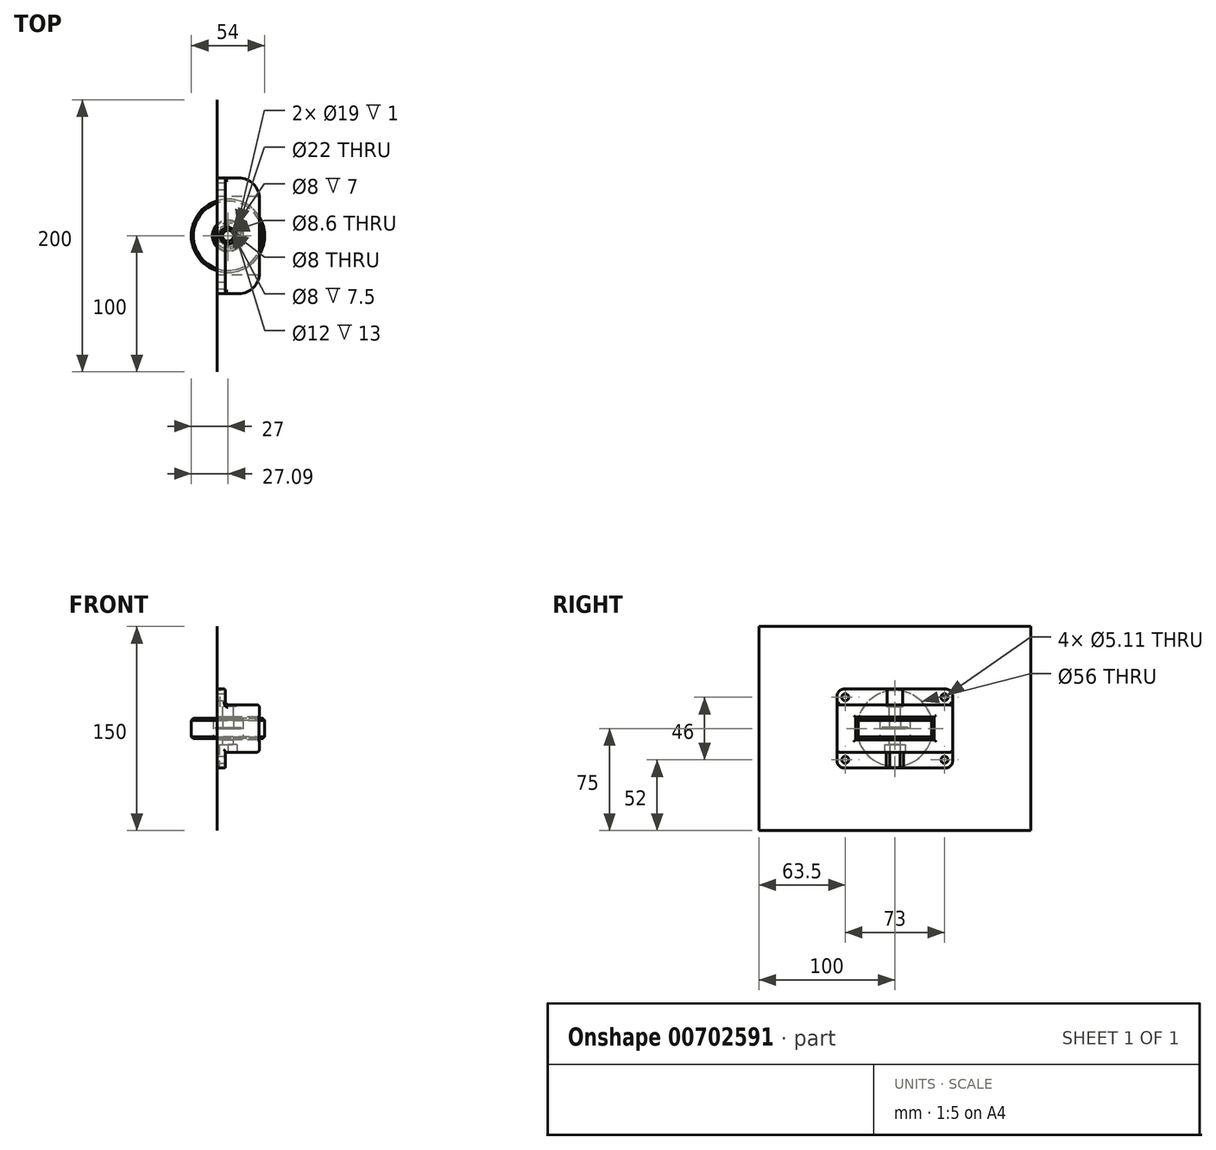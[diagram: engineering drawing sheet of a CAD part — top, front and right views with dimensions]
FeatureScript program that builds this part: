
annotation { "Feature Type Name" : "Feature", "Feature Type Description" : "" }
export const myFeature = defineFeature(function(context is Context, id is Id, definition is map)
    precondition{}
    {
        {
            var Q0;
            Q0=qCreatedBy(makeId("Right.planeOp"),FACE);
            var sketch = newSketch(context, id + "F0", { "sketchPlane" : qUnion([Q0])});
            skLineSegment(sketch, "E0.bottom", {"start": v(100, 75) * mm, "end": v(-100, 75) * mm});
            skLineSegment(sketch, "E0.top", {"start": v(100, -75) * mm, "end": v(-100, -75) * mm});
            skLineSegment(sketch, "E0.left", {"start": v(100, 75) * mm, "end": v(100, -75) * mm});
            skLineSegment(sketch, "E0.right", {"start": v(-100, 75) * mm, "end": v(-100, -75) * mm});
            skPoint(sketch, "E0.middle", {"position": v(0, 0) * mm});
            skCircle(sketch, "E1", {"center": v(0, 0) * mm, "radius": 28 * mm});
            skSolve(sketch);
        }
        {
            var Q0;
            Q0=makeQuery(id+"F0.imprint","IMPRINT",FACE,{"disambiguationData":[TD([[makeQuery(id+"F0.imprint","IMPRINT",EDGE,{"derivedFrom":sQuery(id+"F0.wireOp",EDGE,"E0.bottom")}),1.0]])]});
            extrude(context, id + "F1", {"entities" : qUnion([Q0]), "oppositeDirection" : true, "depth" : 3 / 203.2 * mm, "offsetDistance" : 25 * mm});
        }
        {
            var Q0;
            Q0=qCreatedBy(makeId("Top.planeOp"),FACE);
            var sketch = newSketch(context, id + "F2", { "sketchPlane" : qUnion([Q0])});
            skCircle(sketch, "E2", {"center": v(8, 0) * mm, "radius": 4 * mm});
            skCircle(sketch, "E3", {"center": v(8, 0) * mm, "radius": 11 * mm});
            skLineSegment(sketch, "E4", {"start": v(-49.17, 0) * mm, "end": v(42.17, 0) * mm, "construction": true});
            skLineSegment(sketch, "E5", {"start": v(-9.33, 54.74) * mm, "end": v(-9.33, -36.6) * mm, "construction": true});
            skSolve(sketch);
        }
        {
            var Q0;
            Q0=makeQuery(id+"F2.imprint","IMPRINT",FACE,{"disambiguationData":[TD([[makeQuery(id+"F2.imprint","IMPRINT",EDGE,{"derivedFrom":sQuery(id+"F2.wireOp",EDGE,"E2")}),-1.0]])]});
            extrude(context, id + "F3", {"entities" : qUnion([Q0]), "depth" : 7 * mm, "offsetDistance" : 25 * mm});
        }
        {
            var Q0;
            Q0=makeQuery(id+"F3.opExtrude","CAP_FACE",FACE,{"disambiguationData":[OSD([sQuery(id+"F2.wireOp",EDGE,"E2"),sQuery(id+"F2.wireOp",EDGE,"E3")])],"isStart":false});
            var sketch = newSketch(context, id + "F4", { "sketchPlane" : qUnion([Q0])});
            skCircle(sketch, "E6", {"center": v(8, 0) * mm, "radius": 5.5 * mm});
            skCircle(sketch, "E7", {"center": v(8, 0) * mm, "radius": 9.5 * mm});
            skSolve(sketch);
        }
        {
            var Q0;
            Q0=makeQuery(id+"F4.imprint","IMPRINT",FACE,{"disambiguationData":[TD([[makeQuery(id+"F4.imprint","IMPRINT",EDGE,{"derivedFrom":sQuery(id+"F4.wireOp",EDGE,"E6")}),-1.0]])]});
            extrude(context, id + "F5", {"entities" : qUnion([Q0]), "operationType" : NewBodyOperationType.REMOVE, "oppositeDirection" : true, "depth" : 1 * mm, "offsetDistance" : 25 * mm});
        }
        {
            var Q0;
            Q0=makeQuery(id+"F3.opExtrude","CAP_FACE",FACE,{"disambiguationData":[OSD([sQuery(id+"F2.wireOp",EDGE,"E2"),sQuery(id+"F2.wireOp",EDGE,"E3")])],"isStart":true});
            var sketch = newSketch(context, id + "F6", { "sketchPlane" : qUnion([Q0])});
            skCircle(sketch, "E8", {"center": v(8, 0) * mm, "radius": 5.5 * mm});
            skCircle(sketch, "E9", {"center": v(8, 0) * mm, "radius": 9.5 * mm});
            skSolve(sketch);
        }
        {
            var Q0;
            Q0=makeQuery(id+"F6.imprint","IMPRINT",FACE,{"disambiguationData":[TD([[makeQuery(id+"F6.imprint","IMPRINT",EDGE,{"derivedFrom":sQuery(id+"F6.wireOp",EDGE,"E8")}),-1.0]])]});
            extrude(context, id + "F7", {"entities" : qUnion([Q0]), "operationType" : NewBodyOperationType.REMOVE, "oppositeDirection" : true, "depth" : 1 * mm, "offsetDistance" : 25 * mm});
        }
        {
            var Q0;
            Q0=qCreatedBy(makeId("Top.planeOp"),FACE);
            var sketch = newSketch(context, id + "F8", { "sketchPlane" : qUnion([Q0])});
            skCircle(sketch, "E10", {"center": v(7.9, 0) * mm, "radius": 27 * mm});
            skCircle(sketch, "E11", {"center": v(7.9, 0) * mm, "radius": 11 * mm});
            skSolve(sketch);
        }
        {
            var Q0;
            Q0 = qSketchRegion(id + "F8", true);
            extrude(context, id + "F9", {"entities" : qUnion([Q0]), "endBound" : BoundingType.SYMMETRIC, "depth" : 15 * mm, "offsetDistance" : 25 * mm});
        }
        {
            var Q0;
            Q0=makeQuery(id+"F9.opExtrude","CAP_EDGE",EDGE,{"disambiguationData":[OSD([sQuery(id+"F8.wireOp",EDGE,"E10")])],"isStart":false});
            var Q1;
            Q1=makeQuery(id+"F9.opExtrude","CAP_EDGE",EDGE,{"disambiguationData":[OSD([sQuery(id+"F8.wireOp",EDGE,"E10")])],"isStart":true});
            chamfer(context, id + "F10", {"entities" : qUnion([Q0, Q1]), "width" : 1.5 * mm, "tangentPropagation" : true});
        }
        {
            var Q0;
            Q0=makeQuery(id+"F0.imprint","IMPRINT",FACE,{"disambiguationData":[TD([[makeQuery(id+"F0.imprint","IMPRINT",EDGE,{"derivedFrom":sQuery(id+"F0.wireOp",EDGE,"E0.bottom")}),1.0]])]});
            var sketch = newSketch(context, id + "F11", { "sketchPlane" : qUnion([Q0])});
            skLineSegment(sketch, "E12.bottom", {"start": v(-42.5, 29) * mm, "end": v(42.5, 29) * mm});
            skLineSegment(sketch, "E12.top", {"start": v(-42.5, -29) * mm, "end": v(42.5, -29) * mm});
            skLineSegment(sketch, "E12.left", {"start": v(-42.5, 29) * mm, "end": v(-42.5, -29) * mm});
            skLineSegment(sketch, "E12.right", {"start": v(42.5, 29) * mm, "end": v(42.5, -29) * mm});
            skPoint(sketch, "E12.middle", {"position": v(0, 0) * mm});
            skLineSegment(sketch, "E13.bottom", {"start": v(29, 8.5) * mm, "end": v(-29, 8.5) * mm});
            skLineSegment(sketch, "E13.top", {"start": v(29, -8.5) * mm, "end": v(-29, -8.5) * mm});
            skLineSegment(sketch, "E13.left", {"start": v(29, 8.5) * mm, "end": v(29, -8.5) * mm});
            skLineSegment(sketch, "E13.right", {"start": v(-29, 8.5) * mm, "end": v(-29, -8.5) * mm});
            skSolve(sketch);
        }
        {
            var Q0;
            Q0=makeQuery(id+"F11.imprint","IMPRINT",FACE,{"disambiguationData":[TD([[makeQuery(id+"F11.imprint","IMPRINT",EDGE,{"derivedFrom":sQuery(id+"F11.wireOp",EDGE,"E12.bottom")}),-1.0]])]});
            var Q1;
            {var subQ0=sQuery(id+"F11.wireOp",EDGE,"E13.bottom");var subQ1=makeQuery(id+"F0.imprint","IMPRINT",EDGE,{"derivedFrom":sQuery(id+"F0.wireOp",EDGE,"E1")});var subQ2=makeQuery(id+"F11.imprint","INTERSECT",VERTEX,{"disambiguationData":[OD(0.0)],"derivedFrom":[subQ1,subQ0]});Q1=makeQuery(id+"F11.imprint","IMPRINT",FACE,{"disambiguationData":[TD([[makeQuery(id+"F11.imprint","IMPRINT",EDGE,{"disambiguationData":[TD([[subQ2,-1.0]])],"derivedFrom":subQ0}),-1.0]])]});}
            var Q2;
            {var subQ0=sQuery(id+"F11.wireOp",EDGE,"E13.top");var subQ1=makeQuery(id+"F0.imprint","IMPRINT",EDGE,{"derivedFrom":sQuery(id+"F0.wireOp",EDGE,"E1")});var subQ2=makeQuery(id+"F11.imprint","INTERSECT",VERTEX,{"disambiguationData":[OD(0.0)],"derivedFrom":[subQ1,subQ0]});Q2=makeQuery(id+"F11.imprint","IMPRINT",FACE,{"disambiguationData":[TD([[makeQuery(id+"F11.imprint","IMPRINT",EDGE,{"disambiguationData":[TD([[subQ2,-1.0]])],"derivedFrom":subQ0}),1.0]])]});}
            extrude(context, id + "F12", {"entities" : qUnion([Q0, Q1, Q2]), "depth" : 6 * mm, "offsetDistance" : 25 * mm});
        }
        {
            var Q0;
            Q0=makeQuery(id+"F12.opExtrude","CAP_FACE",FACE,{"disambiguationData":[OSD([sQuery(id+"F11.wireOp",EDGE,"E12.bottom"),sQuery(id+"F11.wireOp",EDGE,"E12.top"),sQuery(id+"F11.wireOp",EDGE,"E12.left"),sQuery(id+"F11.wireOp",EDGE,"E12.right"),sQuery(id+"F11.wireOp",EDGE,"E13.bottom"),sQuery(id+"F11.wireOp",EDGE,"E13.top"),sQuery(id+"F11.wireOp",EDGE,"E13.left"),sQuery(id+"F11.wireOp",EDGE,"E13.right")])],"isStart":false});
            var sketch = newSketch(context, id + "F13", { "sketchPlane" : qUnion([Q0])});
            skLineSegment(sketch, "E14.bottom", {"start": v(-42.5, -17.5) * mm, "end": v(42.5, -17.5) * mm});
            skLineSegment(sketch, "E14.top", {"start": v(-42.5, 17.5) * mm, "end": v(42.5, 17.5) * mm});
            skLineSegment(sketch, "E14.left", {"start": v(-42.5, -17.5) * mm, "end": v(-42.5, 17.5) * mm});
            skLineSegment(sketch, "E14.right", {"start": v(42.5, -17.5) * mm, "end": v(42.5, 17.5) * mm});
            skPoint(sketch, "E14.middle", {"position": v(0, 0) * mm});
            skLineSegment(sketch, "E15.bottom", {"start": v(-36.5, 23) * mm, "end": v(36.5, 23) * mm, "construction": true});
            skLineSegment(sketch, "E15.top", {"start": v(-36.5, -23) * mm, "end": v(36.5, -23) * mm, "construction": true});
            skLineSegment(sketch, "E15.left", {"start": v(-36.5, 23) * mm, "end": v(-36.5, -23) * mm, "construction": true});
            skLineSegment(sketch, "E15.right", {"start": v(36.5, 23) * mm, "end": v(36.5, -23) * mm, "construction": true});
            skSolve(sketch);
        }
        {
            var Q0;
            Q0=makeQuery(id+"F13.imprint","IMPRINT",FACE,{"disambiguationData":[TD([[makeQuery(id+"F13.imprint","IMPRINT",EDGE,{"derivedFrom":sQuery(id+"F13.wireOp",EDGE,"E14.bottom")}),1.0]])]});
            extrude(context, id + "F14", {"entities" : qUnion([Q0]), "operationType" : NewBodyOperationType.ADD, "depth" : 25 * mm, "offsetDistance" : 25 * mm});
        }
        {
            var Q0;
            Q0=makeQuery(id+"F14.opExtrude","CAP_EDGE",EDGE,{"disambiguationData":[OSD([sQuery(id+"F13.wireOp",EDGE,"E14.left")])],"isStart":false});
            var Q1;
            Q1=makeQuery(id+"F14.opExtrude","CAP_EDGE",EDGE,{"disambiguationData":[OSD([sQuery(id+"F13.wireOp",EDGE,"E14.right")])],"isStart":false});
            fillet(context, id + "F15", {"entities" : qUnion([Q0, Q1]), "radius" : 15 * mm, "tangentPropagation" : true, "allowEdgeOverflow" : false});
        }
        {
            var Q0;
            Q0=makeQuery(id+"F14.opExtrude","SWEPT_FACE",FACE,{"disambiguationData":[OSD([sQuery(id+"F13.wireOp",EDGE,"E14.top")])]});
            var sketch = newSketch(context, id + "F16", { "sketchPlane" : qUnion([Q0])});
            skCircle(sketch, "E16", {"center": v(8, 0) * mm, "radius": 4 * mm});
            skSolve(sketch);
        }
        {
            var Q0;
            Q0 = qSketchRegion(id + "F16", true);
            extrude(context, id + "F17", {"entities" : qUnion([Q0]), "operationType" : NewBodyOperationType.REMOVE, "endBound" : BoundingType.THROUGH_ALL, "oppositeDirection" : true, "depth" : 25 * mm, "offsetDistance" : 25 * mm});
        }
        {
            var Q0;
            Q0=makeQuery(id+"F12.opExtrude","SWEPT_FACE",FACE,{"disambiguationData":[OSD([sQuery(id+"F11.wireOp",EDGE,"E12.bottom")])]});
            var sketch = newSketch(context, id + "F18", { "sketchPlane" : qUnion([Q0])});
            skCircle(sketch, "E17", {"center": v(8, 0) * mm, "radius": 6 * mm});
            skSolve(sketch);
        }
        {
            var Q0;
            {var subQ0=sQuery(id+"F18.wireOp",EDGE,"E17");var subQ1=makeQuery(id+"F12.opExtrude","CAP_EDGE",EDGE,{"disambiguationData":[OSD([sQuery(id+"F11.wireOp",EDGE,"E12.bottom")])],"isStart":false});var subQ2=makeQuery(id+"F18.imprint","INTERSECT",VERTEX,{"disambiguationData":[OD(0.0)],"derivedFrom":[subQ1,subQ0]});Q0=makeQuery(id+"F18.imprint","IMPRINT",FACE,{"disambiguationData":[TD([[makeQuery(id+"F18.imprint","IMPRINT",EDGE,{"disambiguationData":[TD([[subQ2,-1.0]])],"derivedFrom":subQ0}),1.0]])]});}
            var Q1;
            {var subQ0=sQuery(id+"F18.wireOp",EDGE,"E17");var subQ1=makeQuery(id+"F12.opExtrude","CAP_EDGE",EDGE,{"disambiguationData":[OSD([sQuery(id+"F11.wireOp",EDGE,"E12.bottom")])],"isStart":false});var subQ2=makeQuery(id+"F18.imprint","INTERSECT",VERTEX,{"disambiguationData":[OD(0.0)],"derivedFrom":[subQ1,subQ0]});Q1=makeQuery(id+"F18.imprint","IMPRINT",FACE,{"disambiguationData":[TD([[makeQuery(id+"F18.imprint","IMPRINT",EDGE,{"disambiguationData":[TD([[subQ2,1.0]])],"derivedFrom":subQ0}),1.0]])]});}
            extrude(context, id + "F19", {"entities" : qUnion([Q0, Q1]), "operationType" : NewBodyOperationType.REMOVE, "oppositeDirection" : true, "depth" : 13 * mm, "offsetDistance" : 25 * mm});
        }
        {
            var Q0;
            Q0=makeQuery(id+"F12.opExtrude","SWEPT_FACE",FACE,{"disambiguationData":[OSD([sQuery(id+"F11.wireOp",EDGE,"E12.top")])]});
            var sketch = newSketch(context, id + "F20", { "sketchPlane" : qUnion([Q0])});
            skCircle(sketch, "E18.cCircle", {"center": v(8, 0) * mm, "radius": 6.5 * mm, "construction": true});
            skLineSegment(sketch, "E18.0", {"start": v(14.5, 3.75) * mm, "end": v(14.5, -3.75) * mm});
            skLineSegment(sketch, "E18.1", {"start": v(14.5, -3.75) * mm, "end": v(8, -7.5) * mm});
            skLineSegment(sketch, "E18.2", {"start": v(8, -7.5) * mm, "end": v(1.5, -3.75) * mm});
            skLineSegment(sketch, "E18.3", {"start": v(1.5, -3.75) * mm, "end": v(1.5, 3.75) * mm});
            skLineSegment(sketch, "E18.4", {"start": v(1.5, 3.75) * mm, "end": v(8, 7.5) * mm});
            skLineSegment(sketch, "E18.5", {"start": v(8, 7.5) * mm, "end": v(14.5, 3.75) * mm});
            skPoint(sketch, "E18.0.midPoint", {"position": v(14.5, 0) * mm});
            skSolve(sketch);
        }
        {
            var Q0;
            Q0 = qSketchRegion(id + "F20", true);
            extrude(context, id + "F21", {"entities" : qUnion([Q0]), "operationType" : NewBodyOperationType.REMOVE, "oppositeDirection" : true, "depth" : 17 * mm, "offsetDistance" : 25 * mm});
        }
        {
            var Q0;
            Q0=sQuery(id+"F13.wireOp",VERTEX,"E15.left.start");
            var Q1;
            Q1=sQuery(id+"F13.wireOp",VERTEX,"E15.right.start");
            var Q2;
            Q2=sQuery(id+"F13.wireOp",VERTEX,"E15.left.end");
            var Q3;
            Q3=sQuery(id+"F13.wireOp",VERTEX,"E15.right.end");
            var Q4;
            Q4=makeQuery(id+"F12.opExtrude","SWEPT_BODY",BODY,{"disambiguationData":[OSD([sQuery(id+"F11.wireOp",EDGE,"E12.bottom"),sQuery(id+"F11.wireOp",EDGE,"E12.top"),sQuery(id+"F11.wireOp",EDGE,"E12.left"),sQuery(id+"F11.wireOp",EDGE,"E12.right"),sQuery(id+"F11.wireOp",EDGE,"E13.bottom"),sQuery(id+"F11.wireOp",EDGE,"E13.top"),sQuery(id+"F11.wireOp",EDGE,"E13.left"),sQuery(id+"F11.wireOp",EDGE,"E13.right")])]});
            hole(context, id + "F22", {"style" : HoleStyle.SIMPLE, "endStyle" : HoleEndStyle.THROUGH, "standardTappedOrClearance" : lookupTablePath({ "standard" : "ANSI", "fit" : "Normal (ASME)", "size" : "#10", "type" : "Clearance" }), "standardBlindInLast" : lookupTablePath({ "fit" : "Free", "standard" : "ANSI", "size" : "#10", "type" : "Clearance" }), "holeDiameter" : 5.1 * mm, "majorDiameter" : 5 * mm, "isTappedThrough" : true, "tappedDepth" : 12 * mm, "tapClearance" : 3, "locations" : qUnion([Q0, Q1, Q2, Q3]), "scope" : qUnion([Q4])});
        }
        {
            var Q0;
            Q0=makeQuery(id+"F12.opExtrude","SWEPT_EDGE",EDGE,{"disambiguationData":[OSD([sQuery(id+"F11.wireOp",EDGE,"E12.bottom"),sQuery(id+"F11.wireOp",EDGE,"E12.left")])]});
            var Q1;
            Q1=makeQuery(id+"F12.opExtrude","SWEPT_EDGE",EDGE,{"disambiguationData":[OSD([sQuery(id+"F11.wireOp",EDGE,"E12.top"),sQuery(id+"F11.wireOp",EDGE,"E12.left")])]});
            var Q2;
            Q2=makeQuery(id+"F12.opExtrude","SWEPT_EDGE",EDGE,{"disambiguationData":[OSD([sQuery(id+"F11.wireOp",EDGE,"E12.top"),sQuery(id+"F11.wireOp",EDGE,"E12.right")])]});
            var Q3;
            Q3=makeQuery(id+"F12.opExtrude","SWEPT_EDGE",EDGE,{"disambiguationData":[OSD([sQuery(id+"F11.wireOp",EDGE,"E12.bottom"),sQuery(id+"F11.wireOp",EDGE,"E12.right")])]});
            fillet(context, id + "F23", {"entities" : qUnion([Q0, Q1, Q2, Q3]), "radius" : 5 * mm, "tangentPropagation" : true, "allowEdgeOverflow" : false});
        }
        {
            var Q0;
            {var subQ0=sQuery(id+"F11.wireOp",EDGE,"E12.right");var subQ1=sQuery(id+"F11.wireOp",EDGE,"E12.bottom");Q0=makeQuery(id+"F19.boolean.opBoolean","SPLIT",EDGE,{"disambiguationData":[TD([makeQuery(id+"F12.opExtrude","SWEPT_FACE",FACE,{"disambiguationData":[OSD([subQ0])]})])],"derivedFrom":makeQuery(id+"F12.opExtrude","CAP_EDGE",EDGE,{"disambiguationData":[OSD([subQ1])],"isStart":false})});}
            var Q1;
            Q1=makeQuery(id+"F19.boolean.opBoolean","COPY",EDGE,{"derivedFrom":makeQuery(id+"F19.opExtrude","CAP_EDGE",EDGE,{"disambiguationData":[OSD([sQuery(id+"F18.wireOp",EDGE,"E17")])],"isStart":true})});
            var Q2;
            {var subQ0=sQuery(id+"F11.wireOp",EDGE,"E12.left");var subQ1=sQuery(id+"F11.wireOp",EDGE,"E12.bottom");Q2=makeQuery(id+"F19.boolean.opBoolean","SPLIT",EDGE,{"disambiguationData":[TD([makeQuery(id+"F12.opExtrude","SWEPT_FACE",FACE,{"disambiguationData":[OSD([subQ0])]})])],"derivedFrom":makeQuery(id+"F12.opExtrude","CAP_EDGE",EDGE,{"disambiguationData":[OSD([subQ1])],"isStart":false})});}
            var Q3;
            {var subQ0=sQuery(id+"F11.wireOp",EDGE,"E12.right");var subQ1=makeQuery(id+"F12.opExtrude","SWEPT_FACE",FACE,{"disambiguationData":[OSD([subQ0])]});var subQ4=sQuery(id+"F11.wireOp",EDGE,"E12.top");var subQ5=makeQuery(id+"F12.opExtrude","SWEPT_FACE",FACE,{"disambiguationData":[OSD([subQ4])]});var subQ6=sQuery(id+"F11.wireOp",EDGE,"E12.left");Q3=makeQuery(id+"F23.opFillet","BLEND_EDGE",EDGE,{"blendedFrom":[makeQuery(id+"F12.opExtrude","SWEPT_EDGE",EDGE,{"disambiguationData":[OSD([subQ4,subQ0])]}),makeQuery(id+"F17.boolean.opBoolean","SPLIT",FACE,{"disambiguationData":[TD([subQ1])],"derivedFrom":makeQuery(id+"F14.boolean.opBoolean","SPLIT",FACE,{"disambiguationData":[TD([subQ5])],"derivedFrom":makeQuery(id+"F12.opExtrude","CAP_FACE",FACE,{"disambiguationData":[OSD([sQuery(id+"F11.wireOp",EDGE,"E12.bottom"),subQ4,subQ6,subQ0,sQuery(id+"F11.wireOp",EDGE,"E13.bottom"),sQuery(id+"F11.wireOp",EDGE,"E13.top"),sQuery(id+"F11.wireOp",EDGE,"E13.left"),sQuery(id+"F11.wireOp",EDGE,"E13.right")])],"isStart":false})})})],"blendedInto":[makeQuery(id+"F17.boolean.opBoolean","SPLIT",FACE,{"disambiguationData":[TD([subQ1])],"derivedFrom":makeQuery(id+"F14.boolean.opBoolean","SPLIT",FACE,{"disambiguationData":[TD([subQ5])],"derivedFrom":makeQuery(id+"F12.opExtrude","CAP_FACE",FACE,{"disambiguationData":[OSD([sQuery(id+"F11.wireOp",EDGE,"E12.bottom"),subQ4,subQ6,subQ0,sQuery(id+"F11.wireOp",EDGE,"E13.bottom"),sQuery(id+"F11.wireOp",EDGE,"E13.top"),sQuery(id+"F11.wireOp",EDGE,"E13.left"),sQuery(id+"F11.wireOp",EDGE,"E13.right")])],"isStart":false})})})]});}
            var Q4;
            {var subQ0=sQuery(id+"F11.wireOp",EDGE,"E12.left");var subQ1=sQuery(id+"F11.wireOp",EDGE,"E12.top");Q4=makeQuery(id+"F17.boolean.opBoolean","SPLIT",EDGE,{"disambiguationData":[TD([makeQuery(id+"F12.opExtrude","SWEPT_FACE",FACE,{"disambiguationData":[OSD([subQ0])]})])],"derivedFrom":makeQuery(id+"F12.opExtrude","CAP_EDGE",EDGE,{"disambiguationData":[OSD([subQ1])],"isStart":false})});}
            var Q5;
            Q5=makeQuery(id+"F21.boolean.opBoolean","COPY",EDGE,{"derivedFrom":makeQuery(id+"F21.opExtrude","CAP_EDGE",EDGE,{"disambiguationData":[OSD([sQuery(id+"F20.wireOp",EDGE,"E18.4")])],"isStart":true})});
            var Q6;
            Q6=makeQuery(id+"F21.boolean.opBoolean","COPY",EDGE,{"derivedFrom":makeQuery(id+"F21.opExtrude","CAP_EDGE",EDGE,{"disambiguationData":[OSD([sQuery(id+"F20.wireOp",EDGE,"E18.3")])],"isStart":true})});
            var Q7;
            Q7=makeQuery(id+"F21.boolean.opBoolean","COPY",EDGE,{"derivedFrom":makeQuery(id+"F21.opExtrude","CAP_EDGE",EDGE,{"disambiguationData":[OSD([sQuery(id+"F20.wireOp",EDGE,"E18.2")])],"isStart":true})});
            var Q8;
            {var subQ0=sQuery(id+"F11.wireOp",EDGE,"E13.left");Q8=makeQuery(id+"F15.opFillet","BLEND_EDGE",EDGE,{"blendedFrom":[makeQuery(id+"F14.opExtrude","CAP_EDGE",EDGE,{"disambiguationData":[OSD([sQuery(id+"F13.wireOp",EDGE,"E14.right")])],"isStart":false}),makeQuery(id+"F14.boolean.opBoolean","MERGE",FACE,{"derivedFrom":[makeQuery(id+"F12.opExtrude","SWEPT_FACE",FACE,{"disambiguationData":[OSD([subQ0])]}),makeQuery(id+"F14.opExtrude","SWEPT_FACE",FACE,{"disambiguationData":[OSD([subQ0])]})]})],"blendedInto":[makeQuery(id+"F14.boolean.opBoolean","MERGE",FACE,{"derivedFrom":[makeQuery(id+"F12.opExtrude","SWEPT_FACE",FACE,{"disambiguationData":[OSD([subQ0])]}),makeQuery(id+"F14.opExtrude","SWEPT_FACE",FACE,{"disambiguationData":[OSD([subQ0])]})]})]});}
            var Q9;
            Q9=makeQuery(id+"F14.opExtrude","CAP_EDGE",EDGE,{"disambiguationData":[OSD([sQuery(id+"F11.wireOp",EDGE,"E13.bottom")])],"isStart":false});
            var Q10;
            {var subQ0=sQuery(id+"F11.wireOp",EDGE,"E13.right");Q10=makeQuery(id+"F15.opFillet","BLEND_EDGE",EDGE,{"blendedFrom":[makeQuery(id+"F14.opExtrude","CAP_EDGE",EDGE,{"disambiguationData":[OSD([sQuery(id+"F13.wireOp",EDGE,"E14.left")])],"isStart":false}),makeQuery(id+"F14.boolean.opBoolean","MERGE",FACE,{"derivedFrom":[makeQuery(id+"F12.opExtrude","SWEPT_FACE",FACE,{"disambiguationData":[OSD([subQ0])]}),makeQuery(id+"F14.opExtrude","SWEPT_FACE",FACE,{"disambiguationData":[OSD([subQ0])]})]})],"blendedInto":[makeQuery(id+"F14.boolean.opBoolean","MERGE",FACE,{"derivedFrom":[makeQuery(id+"F12.opExtrude","SWEPT_FACE",FACE,{"disambiguationData":[OSD([subQ0])]}),makeQuery(id+"F14.opExtrude","SWEPT_FACE",FACE,{"disambiguationData":[OSD([subQ0])]})]})]});}
            var Q11;
            Q11=makeQuery(id+"F14.opExtrude","CAP_EDGE",EDGE,{"disambiguationData":[OSD([sQuery(id+"F11.wireOp",EDGE,"E13.top")])],"isStart":false});
            fillet(context, id + "F24", {"entities" : qUnion([Q0, Q1, Q2, Q3, Q4, Q5, Q6, Q7, Q8, Q9, Q10, Q11]), "radius" : 1 * mm, "tangentPropagation" : true, "allowEdgeOverflow" : false});
        }
        {
            var Q0;
            {var subQ0=sQuery(id+"F13.wireOp",EDGE,"E14.bottom");var subQ1=sQuery(id+"F11.wireOp",EDGE,"E12.left");Q0=makeQuery(id+"F17.boolean.opBoolean","SPLIT",EDGE,{"disambiguationData":[TD([makeQuery(id+"F12.opExtrude","SWEPT_FACE",FACE,{"disambiguationData":[OSD([subQ1])]})])],"derivedFrom":makeQuery(id+"F14.opExtrude","CAP_EDGE",EDGE,{"disambiguationData":[OSD([subQ0])],"isStart":true})});}
            var Q1;
            {var subQ0=sQuery(id+"F13.wireOp",EDGE,"E14.bottom");var subQ1=sQuery(id+"F11.wireOp",EDGE,"E12.right");Q1=makeQuery(id+"F17.boolean.opBoolean","SPLIT",EDGE,{"disambiguationData":[TD([makeQuery(id+"F12.opExtrude","SWEPT_FACE",FACE,{"disambiguationData":[OSD([subQ1])]})])],"derivedFrom":makeQuery(id+"F14.opExtrude","CAP_EDGE",EDGE,{"disambiguationData":[OSD([subQ0])],"isStart":true})});}
            var Q2;
            Q2=makeQuery(id+"F14.opExtrude","CAP_EDGE",EDGE,{"disambiguationData":[OSD([sQuery(id+"F13.wireOp",EDGE,"E14.bottom")])],"isStart":false});
            var Q3;
            Q3=makeQuery(id+"F15.opFillet","BLEND_EDGE",EDGE,{"blendedFrom":[makeQuery(id+"F14.opExtrude","CAP_EDGE",EDGE,{"disambiguationData":[OSD([sQuery(id+"F13.wireOp",EDGE,"E14.right")])],"isStart":false}),makeQuery(id+"F14.opExtrude","SWEPT_FACE",FACE,{"disambiguationData":[OSD([sQuery(id+"F13.wireOp",EDGE,"E14.bottom")])]})],"blendedInto":[makeQuery(id+"F14.opExtrude","SWEPT_FACE",FACE,{"disambiguationData":[OSD([sQuery(id+"F13.wireOp",EDGE,"E14.bottom")])]})]});
            var Q4;
            Q4=makeQuery(id+"F15.opFillet","BLEND_EDGE",EDGE,{"blendedFrom":[makeQuery(id+"F14.opExtrude","CAP_EDGE",EDGE,{"disambiguationData":[OSD([sQuery(id+"F13.wireOp",EDGE,"E14.left")])],"isStart":false}),makeQuery(id+"F14.opExtrude","SWEPT_FACE",FACE,{"disambiguationData":[OSD([sQuery(id+"F13.wireOp",EDGE,"E14.bottom")])]})],"blendedInto":[makeQuery(id+"F14.opExtrude","SWEPT_FACE",FACE,{"disambiguationData":[OSD([sQuery(id+"F13.wireOp",EDGE,"E14.bottom")])]})]});
            var Q5;
            {var subQ0=sQuery(id+"F13.wireOp",EDGE,"E14.top");var subQ1=makeQuery(id+"F14.opExtrude","SWEPT_FACE",FACE,{"disambiguationData":[OSD([subQ0])]});var subQ2=sQuery(id+"F11.wireOp",EDGE,"E12.left");var subQ3=makeQuery(id+"F12.opExtrude","CAP_FACE",FACE,{"disambiguationData":[OSD([sQuery(id+"F11.wireOp",EDGE,"E12.bottom"),sQuery(id+"F11.wireOp",EDGE,"E12.top"),subQ2,sQuery(id+"F11.wireOp",EDGE,"E12.right"),sQuery(id+"F11.wireOp",EDGE,"E13.bottom"),sQuery(id+"F11.wireOp",EDGE,"E13.top"),sQuery(id+"F11.wireOp",EDGE,"E13.left"),sQuery(id+"F11.wireOp",EDGE,"E13.right")])],"isStart":false});Q5=makeQuery(id+"F17.boolean.opBoolean","SPLIT",EDGE,{"disambiguationData":[topologyDisambiguationEdgeConnected([subQ3,subQ1]),TD([makeQuery(id+"F12.opExtrude","SWEPT_FACE",FACE,{"disambiguationData":[OSD([subQ2])]})])],"derivedFrom":makeQuery(id+"F14.opExtrude","CAP_EDGE",EDGE,{"disambiguationData":[OSD([subQ0])],"isStart":true})});}
            var Q6;
            {var subQ0=sQuery(id+"F13.wireOp",EDGE,"E14.top");var subQ1=makeQuery(id+"F14.opExtrude","SWEPT_FACE",FACE,{"disambiguationData":[OSD([subQ0])]});var subQ2=sQuery(id+"F11.wireOp",EDGE,"E12.right");var subQ3=makeQuery(id+"F12.opExtrude","CAP_FACE",FACE,{"disambiguationData":[OSD([sQuery(id+"F11.wireOp",EDGE,"E12.bottom"),sQuery(id+"F11.wireOp",EDGE,"E12.top"),sQuery(id+"F11.wireOp",EDGE,"E12.left"),subQ2,sQuery(id+"F11.wireOp",EDGE,"E13.bottom"),sQuery(id+"F11.wireOp",EDGE,"E13.top"),sQuery(id+"F11.wireOp",EDGE,"E13.left"),sQuery(id+"F11.wireOp",EDGE,"E13.right")])],"isStart":false});Q6=makeQuery(id+"F17.boolean.opBoolean","SPLIT",EDGE,{"disambiguationData":[topologyDisambiguationEdgeConnected([subQ3,subQ1]),TD([makeQuery(id+"F12.opExtrude","SWEPT_FACE",FACE,{"disambiguationData":[OSD([subQ2])]})])],"derivedFrom":makeQuery(id+"F14.opExtrude","CAP_EDGE",EDGE,{"disambiguationData":[OSD([subQ0])],"isStart":true})});}
            var Q7;
            Q7=makeQuery(id+"F14.opExtrude","CAP_EDGE",EDGE,{"disambiguationData":[OSD([sQuery(id+"F13.wireOp",EDGE,"E14.top")])],"isStart":false});
            var Q8;
            Q8=makeQuery(id+"F15.opFillet","BLEND_EDGE",EDGE,{"blendedFrom":[makeQuery(id+"F14.opExtrude","CAP_EDGE",EDGE,{"disambiguationData":[OSD([sQuery(id+"F13.wireOp",EDGE,"E14.left")])],"isStart":false}),makeQuery(id+"F14.opExtrude","SWEPT_FACE",FACE,{"disambiguationData":[OSD([sQuery(id+"F13.wireOp",EDGE,"E14.top")])]})],"blendedInto":[makeQuery(id+"F14.opExtrude","SWEPT_FACE",FACE,{"disambiguationData":[OSD([sQuery(id+"F13.wireOp",EDGE,"E14.top")])]})]});
            fillet(context, id + "F25", {"entities" : qUnion([Q0, Q1, Q2, Q3, Q4, Q5, Q6, Q7, Q8]), "radius" : 2 * mm, "tangentPropagation" : true, "allowEdgeOverflow" : false});
        }
        {
            var Q0;
            {var subQ0=sQuery(id+"F2.wireOp",EDGE,"E2");Q0=makeQuery(id+"F5.boolean.opBoolean","SPLIT",FACE,{"disambiguationData":[TD([makeQuery(id+"F3.opExtrude","SWEPT_FACE",FACE,{"disambiguationData":[OSD([subQ0])]})])],"derivedFrom":makeQuery(id+"F3.opExtrude","CAP_FACE",FACE,{"disambiguationData":[OSD([subQ0,sQuery(id+"F2.wireOp",EDGE,"E3")])],"isStart":false})});}
            var sketch = newSketch(context, id + "F26", { "sketchPlane" : qUnion([Q0])});
            skCircle(sketch, "E19", {"center": v(8, 0) * mm, "radius": 8 * mm});
            skCircle(sketch, "E20", {"center": v(8, 0) * mm, "radius": 4.3 * mm});
            skSolve(sketch);
        }
        {
            var Q0;
            Q0 = qSketchRegion(id + "F26", true);
            extrude(context, id + "F27", {"entities" : qUnion([Q0]), "depth" : 1 * mm, "offsetDistance" : 25 * mm});
        }
        {
            var Q0;
            Q0=makeQuery(id+"F9.opExtrude","CAP_EDGE",EDGE,{"disambiguationData":[OSD([sQuery(id+"F8.wireOp",EDGE,"E11")])],"isStart":false});
            var Q1;
            Q1=makeQuery(id+"F9.opExtrude","CAP_EDGE",EDGE,{"disambiguationData":[OSD([sQuery(id+"F8.wireOp",EDGE,"E11")])],"isStart":true});
            chamfer(context, id + "F28", {"entities" : qUnion([Q0, Q1]), "width" : 0.5 * mm, "tangentPropagation" : true});
        }
    });
